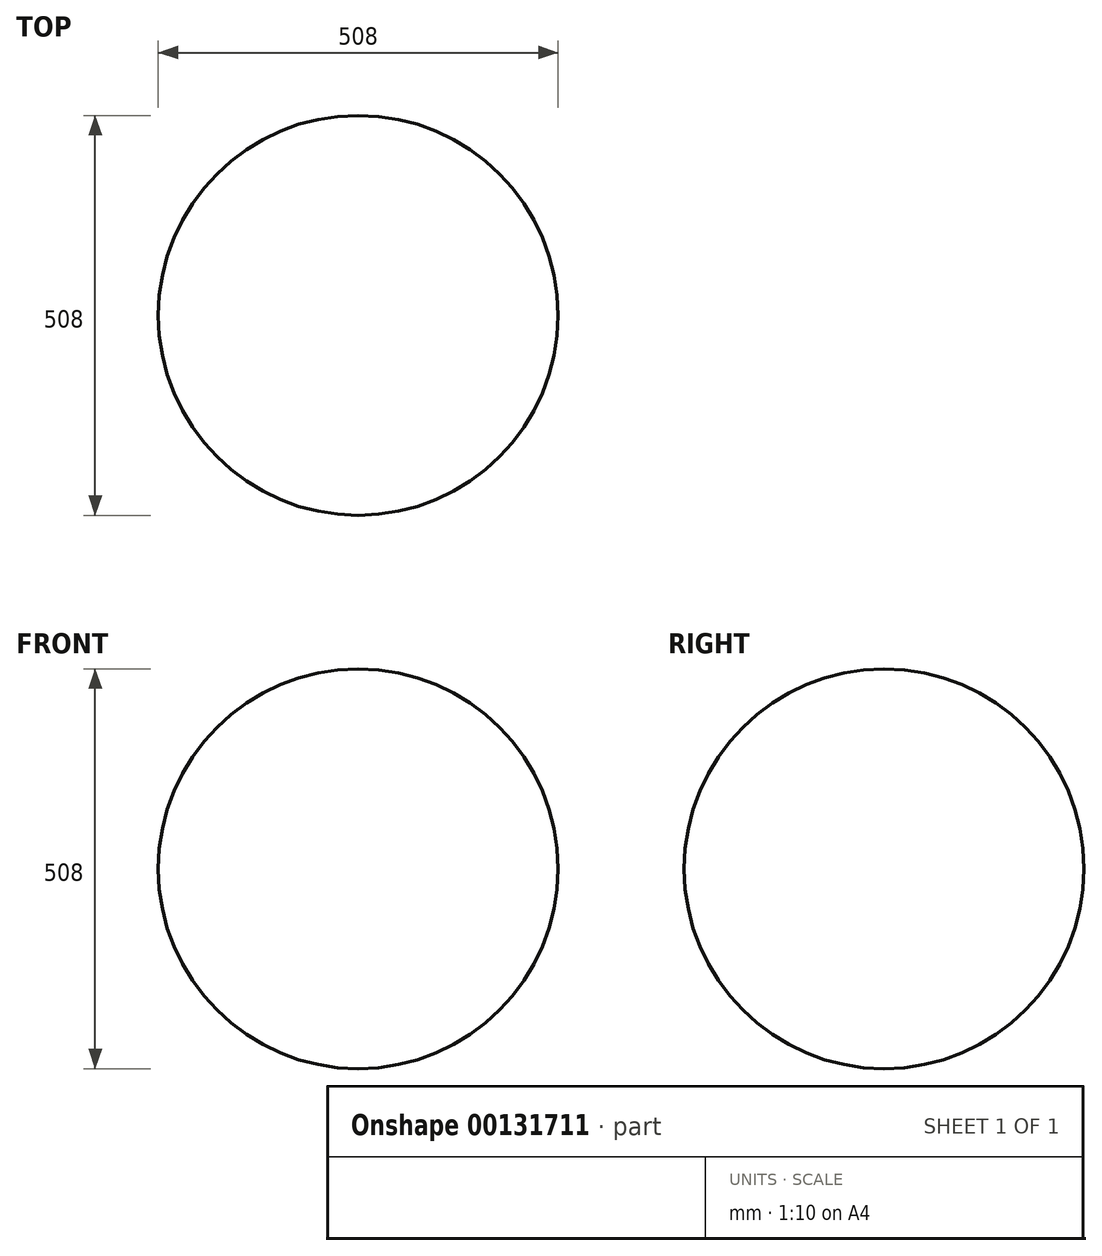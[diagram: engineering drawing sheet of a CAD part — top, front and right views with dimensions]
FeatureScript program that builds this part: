
annotation { "Feature Type Name" : "Feature", "Feature Type Description" : "" }
export const myFeature = defineFeature(function(context is Context, id is Id, definition is map)
    precondition{}
    {
        {
            var Q0;
            Q0=qCreatedBy(makeId("Front.planeOp"),FACE);
            var sketch = newSketch(context, id + "F0", { "sketchPlane" : qUnion([Q0])});
            skCircle(sketch, "E0", {"center": v(0, 0) * mm, "radius": 254 * mm});
            skLineSegment(sketch, "E1", {"start": v(0, 254) * mm, "end": v(0, -254) * mm});
            skSolve(sketch);
        }
        {
            var Q0;
            {var subQ0=sQuery(id+"F0.wireOp",EDGE,"E1");Q0=makeQuery(id+"F0.imprint","IMPRINT",FACE,{"disambiguationData":[TD([[makeQuery(id+"F0.imprint","IMPRINT",EDGE,{"derivedFrom":subQ0}),-1.0]])]});}
            var Q1;
            Q1=sQuery(id+"F0.wireOp",EDGE,"E1");
            revolve(context, id + "F1", {"entities" : qUnion([Q0]), "axis" : qUnion([Q1]), "revolveType" : RevolveType.FULL});
        }
    });
